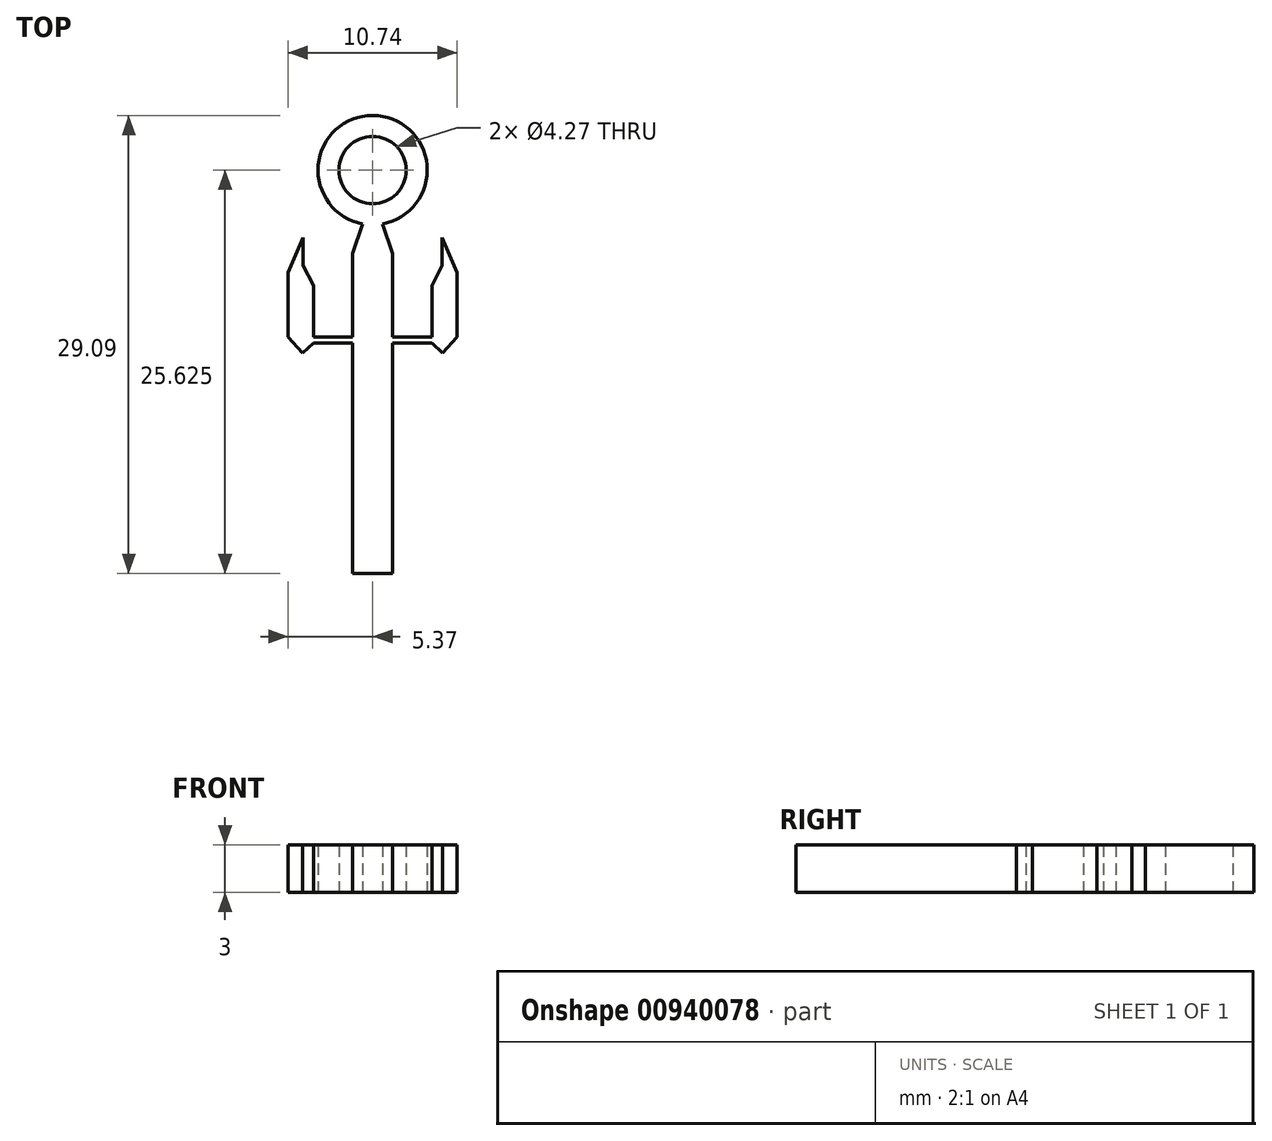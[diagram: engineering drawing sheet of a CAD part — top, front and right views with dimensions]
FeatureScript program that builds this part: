
annotation { "Feature Type Name" : "Feature", "Feature Type Description" : "" }
export const myFeature = defineFeature(function(context is Context, id is Id, definition is map)
    precondition{}
    {
        {
            var Q0;
            Q0=qCreatedBy(makeId("Top.planeOp"),FACE);
            var sketch = newSketch(context, id + "F0", { "sketchPlane" : qUnion([Q0])});
            skLineSegment(sketch, "E0.top", {"start": v(-1.27, -7.52) * mm, "end": v(0, -7.52) * mm});
            skLineSegment(sketch, "E0.left", {"start": v(-1.27, 7.1) * mm, "end": v(-1.27, -7.52) * mm});
            skPoint(sketch, "E0.middle", {"position": v(0, 0) * mm});
            skLineSegment(sketch, "E1", {"start": v(-1.27, 7.52) * mm, "end": v(-3.76, 7.52) * mm});
            skLineSegment(sketch, "E2", {"start": v(-3.76, 7.52) * mm, "end": v(-3.76, 10.76) * mm});
            skLineSegment(sketch, "E3", {"start": v(-3.76, 10.76) * mm, "end": v(-4.42, 12.04) * mm});
            skLineSegment(sketch, "E4", {"start": v(-4.42, 12.04) * mm, "end": v(-4.42, 13.83) * mm});
            skLineSegment(sketch, "E5", {"start": v(-4.42, 13.83) * mm, "end": v(-5.37, 11.61) * mm});
            skPoint(sketch, "E6.startSnap0", {"position": v(0, -7.52) * mm});
            skLineSegment(sketch, "E7", {"start": v(-5.37, 11.61) * mm, "end": v(-5.37, 7.52) * mm});
            skLineSegment(sketch, "E8", {"start": v(-5.37, 7.52) * mm, "end": v(-4.45, 6.5) * mm});
            skLineSegment(sketch, "E9", {"start": v(-4.45, 6.5) * mm, "end": v(-3.76, 7.1) * mm});
            skLineSegment(sketch, "E10", {"start": v(-3.76, 7.1) * mm, "end": v(-1.27, 7.1) * mm});
            skLineSegment(sketch, "E11", {"start": v(-1.27, 7.52) * mm, "end": v(-1.27, 12.8) * mm});
            skLineSegment(sketch, "E12", {"start": v(-1.27, 12.8) * mm, "end": v(-0.63, 14.7) * mm});
            skPoint(sketch, "E13.orphan", {"position": v(1.27, 7.52) * mm});
            skPoint(sketch, "E14.orphan", {"position": v(1.27, -7.52) * mm});
            skLineSegment(sketch, "E15.MirrorCS", {"start": v(3.76, 10.76) * mm, "end": v(4.42, 12.04) * mm});
            skLineSegment(sketch, "E16.MirrorCS", {"start": v(4.45, 6.5) * mm, "end": v(3.76, 7.1) * mm});
            skLineSegment(sketch, "E17.MirrorCS", {"start": v(1.27, -7.52) * mm, "end": v(0, -7.52) * mm});
            skLineSegment(sketch, "E18.MirrorCS", {"start": v(1.27, 12.8) * mm, "end": v(0.63, 14.7) * mm});
            skPoint(sketch, "E19.MirrorP", {"position": v(-1.27, 7.52) * mm});
            skLineSegment(sketch, "E20.MirrorCS", {"start": v(5.37, 11.61) * mm, "end": v(5.37, 7.52) * mm});
            skLineSegment(sketch, "E21.MirrorCS", {"start": v(3.76, 7.52) * mm, "end": v(3.76, 10.76) * mm});
            skPoint(sketch, "E22.MirrorP", {"position": v(-1.27, -7.52) * mm});
            skLineSegment(sketch, "E23.MirrorCS", {"start": v(3.76, 7.1) * mm, "end": v(1.27, 7.1) * mm});
            skLineSegment(sketch, "E24.MirrorCS", {"start": v(1.27, 7.52) * mm, "end": v(3.76, 7.52) * mm});
            skLineSegment(sketch, "E25.MirrorCS", {"start": v(5.37, 7.52) * mm, "end": v(4.45, 6.5) * mm});
            skLineSegment(sketch, "E26.MirrorCS", {"start": v(4.42, 13.83) * mm, "end": v(5.37, 11.61) * mm});
            skLineSegment(sketch, "E27.MirrorCS", {"start": v(1.27, 7.1) * mm, "end": v(1.27, -7.52) * mm});
            skLineSegment(sketch, "E28.MirrorCS", {"start": v(1.27, 7.52) * mm, "end": v(1.27, 12.8) * mm});
            skLineSegment(sketch, "E29.MirrorCS", {"start": v(4.42, 12.04) * mm, "end": v(4.42, 13.83) * mm});
            skPoint(sketch, "E0.bottom.end.orphan", {"position": v(0, 7.52) * mm});
            skArc(sketch, "E30", {"start": v(0.63, 14.7) * mm, "mid": v(0, 21.57) * mm, "end": v(-0.63, 14.7) * mm});
            skCircle(sketch, "E31", {"center": v(0, 18.1) * mm, "radius": 2.14 * mm});
            skPoint(sketch, "E32.orphan", {"position": v(0, 16.52) * mm});
            skPoint(sketch, "E6.start.orphan", {"position": v(0, -8.9) * mm});
            skSolve(sketch);
        }
        {
            var Q0;
            Q0=makeQuery(id+"F0.imprint","IMPRINT",FACE,{"disambiguationData":[TD([[makeQuery(id+"F0.imprint","IMPRINT",EDGE,{"derivedFrom":sQuery(id+"F0.wireOp",EDGE,"E0.top")}),1.0]])]});
            extrude(context, id + "F1", {"entities" : qUnion([Q0]), "depth" : 3 * mm, "offsetDistance" : 25.4 * mm});
        }
    });
